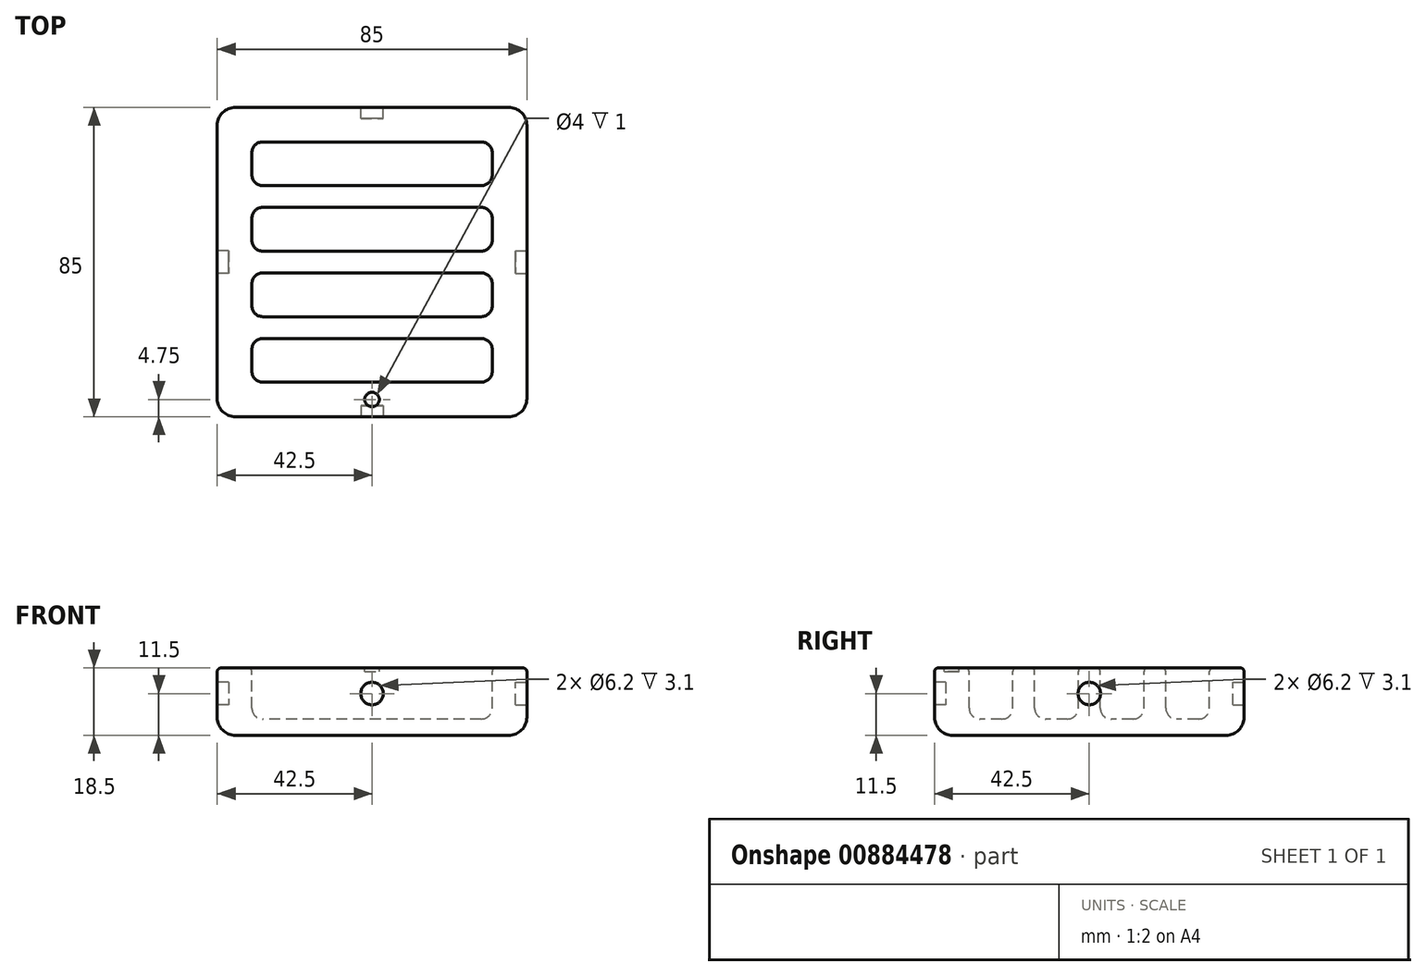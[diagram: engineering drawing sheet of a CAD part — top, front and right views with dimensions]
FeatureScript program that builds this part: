
annotation { "Feature Type Name" : "Feature", "Feature Type Description" : "" }
export const myFeature = defineFeature(function(context is Context, id is Id, definition is map)
    precondition{}
    {
        {
            var Q0;
            Q0=qCreatedBy(makeId("Top.planeOp"),FACE);
            var sketch = newSketch(context, id + "F0", { "sketchPlane" : qUnion([Q0])});
            skLineSegment(sketch, "E0.bottom", {"start": v(-42.5, 42.5) * mm, "end": v(42.5, 42.5) * mm});
            skLineSegment(sketch, "E0.top", {"start": v(-42.5, -42.5) * mm, "end": v(42.5, -42.5) * mm});
            skLineSegment(sketch, "E0.left", {"start": v(-42.5, 42.5) * mm, "end": v(-42.5, -42.5) * mm});
            skLineSegment(sketch, "E0.right", {"start": v(42.5, 42.5) * mm, "end": v(42.5, -42.5) * mm});
            skLineSegment(sketch, "E1.bottom", {"start": v(-30, 33) * mm, "end": v(30, 33) * mm});
            skLineSegment(sketch, "E1.top", {"start": v(-30, 21) * mm, "end": v(30, 21) * mm});
            skLineSegment(sketch, "E1.left", {"start": v(-33, 30) * mm, "end": v(-33, 24) * mm});
            skLineSegment(sketch, "E1.right", {"start": v(33, 30) * mm, "end": v(33, 24) * mm});
            skLineSegment(sketch, "E2.direction1", {"start": v(-33, 21) * mm, "end": v(-9.74, 21) * mm, "construction": true});
            skPoint(sketch, "E3.visualSharp", {"position": v(-33, 33) * mm});
            skArc(sketch, "E3.filletArc", {"start": v(-30, 33) * mm, "mid": v(-32.12, 32.12) * mm, "end": v(-33, 30) * mm});
            skPoint(sketch, "E4.visualSharp", {"position": v(33, 33) * mm});
            skArc(sketch, "E4.filletArc", {"start": v(33, 30) * mm, "mid": v(32.12, 32.12) * mm, "end": v(30, 33) * mm});
            skPoint(sketch, "E5.visualSharp", {"position": v(33, 21) * mm});
            skArc(sketch, "E5.filletArc", {"start": v(30, 21) * mm, "mid": v(32.12, 21.88) * mm, "end": v(33, 24) * mm});
            skPoint(sketch, "E6.visualSharp", {"position": v(-33, 21) * mm});
            skArc(sketch, "E6.filletArc", {"start": v(-33, 24) * mm, "mid": v(-32.12, 21.88) * mm, "end": v(-30, 21) * mm});
            skPoint(sketch, "E7.0.1.0", {"position": v(-33, 15) * mm});
            skLineSegment(sketch, "E7.0.1.1", {"start": v(-33, 3) * mm, "end": v(-9.74, 3) * mm, "construction": true});
            skLineSegment(sketch, "E7.0.1.2", {"start": v(-33, 12) * mm, "end": v(-33, 6) * mm});
            skPoint(sketch, "E7.0.1.3", {"position": v(33, 3) * mm});
            skArc(sketch, "E7.0.1.4", {"start": v(33, 12) * mm, "mid": v(32.12, 14.12) * mm, "end": v(30, 15) * mm});
            skLineSegment(sketch, "E7.0.1.5", {"start": v(-30, 15) * mm, "end": v(30, 15) * mm});
            skArc(sketch, "E7.0.1.6", {"start": v(-30, 15) * mm, "mid": v(-32.12, 14.12) * mm, "end": v(-33, 12) * mm});
            skLineSegment(sketch, "E7.0.1.7", {"start": v(33, 12) * mm, "end": v(33, 6) * mm});
            skPoint(sketch, "E7.0.1.8", {"position": v(33, 15) * mm});
            skLineSegment(sketch, "E7.0.1.9", {"start": v(-30, 3) * mm, "end": v(30, 3) * mm});
            skPoint(sketch, "E7.0.1.10", {"position": v(-33, 3) * mm});
            skArc(sketch, "E7.0.1.11", {"start": v(30, 3) * mm, "mid": v(32.12, 3.88) * mm, "end": v(33, 6) * mm});
            skArc(sketch, "E7.0.1.12", {"start": v(-33, 6) * mm, "mid": v(-32.12, 3.88) * mm, "end": v(-30, 3) * mm});
            skPoint(sketch, "E7.0.2.0", {"position": v(-33, -3) * mm});
            skLineSegment(sketch, "E7.0.2.1", {"start": v(-33, -15) * mm, "end": v(-9.74, -15) * mm, "construction": true});
            skLineSegment(sketch, "E7.0.2.2", {"start": v(-33, -6) * mm, "end": v(-33, -12) * mm});
            skPoint(sketch, "E7.0.2.3", {"position": v(33, -15) * mm});
            skArc(sketch, "E7.0.2.4", {"start": v(33, -6) * mm, "mid": v(32.12, -3.88) * mm, "end": v(30, -3) * mm});
            skLineSegment(sketch, "E7.0.2.5", {"start": v(-30, -3) * mm, "end": v(30, -3) * mm});
            skArc(sketch, "E7.0.2.6", {"start": v(-30, -3) * mm, "mid": v(-32.12, -3.88) * mm, "end": v(-33, -6) * mm});
            skLineSegment(sketch, "E7.0.2.7", {"start": v(33, -6) * mm, "end": v(33, -12) * mm});
            skPoint(sketch, "E7.0.2.8", {"position": v(33, -3) * mm});
            skLineSegment(sketch, "E7.0.2.9", {"start": v(-30, -15) * mm, "end": v(30, -15) * mm});
            skPoint(sketch, "E7.0.2.10", {"position": v(-33, -15) * mm});
            skArc(sketch, "E7.0.2.11", {"start": v(30, -15) * mm, "mid": v(32.12, -14.12) * mm, "end": v(33, -12) * mm});
            skArc(sketch, "E7.0.2.12", {"start": v(-33, -12) * mm, "mid": v(-32.12, -14.12) * mm, "end": v(-30, -15) * mm});
            skPoint(sketch, "E7.0.3.0", {"position": v(-33, -21) * mm});
            skLineSegment(sketch, "E7.0.3.1", {"start": v(-33, -33) * mm, "end": v(-9.74, -33) * mm, "construction": true});
            skLineSegment(sketch, "E7.0.3.2", {"start": v(-33, -24) * mm, "end": v(-33, -30) * mm});
            skPoint(sketch, "E7.0.3.3", {"position": v(33, -33) * mm});
            skArc(sketch, "E7.0.3.4", {"start": v(33, -24) * mm, "mid": v(32.12, -21.88) * mm, "end": v(30, -21) * mm});
            skLineSegment(sketch, "E7.0.3.5", {"start": v(-30, -21) * mm, "end": v(30, -21) * mm});
            skArc(sketch, "E7.0.3.6", {"start": v(-30, -21) * mm, "mid": v(-32.12, -21.88) * mm, "end": v(-33, -24) * mm});
            skLineSegment(sketch, "E7.0.3.7", {"start": v(33, -24) * mm, "end": v(33, -30) * mm});
            skPoint(sketch, "E7.0.3.8", {"position": v(33, -21) * mm});
            skLineSegment(sketch, "E7.0.3.9", {"start": v(-30, -33) * mm, "end": v(30, -33) * mm});
            skPoint(sketch, "E7.0.3.10", {"position": v(-33, -33) * mm});
            skArc(sketch, "E7.0.3.11", {"start": v(30, -33) * mm, "mid": v(32.12, -32.12) * mm, "end": v(33, -30) * mm});
            skArc(sketch, "E7.0.3.12", {"start": v(-33, -30) * mm, "mid": v(-32.12, -32.12) * mm, "end": v(-30, -33) * mm});
            skLineSegment(sketch, "E7.direction1", {"start": v(-33, 21) * mm, "end": v(-8, 21) * mm, "construction": true});
            skLineSegment(sketch, "E7.direction2", {"start": v(-33, 21) * mm, "end": v(-33, 3) * mm, "construction": true});
            skLineSegment(sketch, "E8", {"start": v(-42.5, 0) * mm, "end": v(42.5, 0) * mm, "construction": true});
            skLineSegment(sketch, "E9", {"start": v(0, -42.5) * mm, "end": v(0, 42.5) * mm, "construction": true});
            skCircle(sketch, "E10", {"center": v(0, -37.75) * mm, "radius": 2 * mm});
            skSolve(sketch);
        }
        {
            assignVariable(context, id + "F1", {"name" : "h", "anyValue" : 18.5});
        }
        {
            assignVariable(context, id + "F2", {"name" : "d", "anyValue" : 14});
        }
        {
            var Q0;
            Q0=makeQuery(id+"F0.imprint","IMPRINT",FACE,{"disambiguationData":[TD([[makeQuery(id+"F0.imprint","IMPRINT",EDGE,{"derivedFrom":sQuery(id+"F0.wireOp",EDGE,"E1.bottom")}),-1.0]])]});
            var Q1;
            Q1=makeQuery(id+"F0.imprint","IMPRINT",FACE,{"disambiguationData":[TD([[makeQuery(id+"F0.imprint","IMPRINT",EDGE,{"derivedFrom":sQuery(id+"F0.wireOp",EDGE,"E0.bottom")}),-1.0]])]});
            var Q2;
            Q2=makeQuery(id+"F0.imprint","IMPRINT",FACE,{"disambiguationData":[TD([[makeQuery(id+"F0.imprint","IMPRINT",EDGE,{"derivedFrom":sQuery(id+"F0.wireOp",EDGE,"E2.0.2.0")}),1.0]])]});
            var Q3;
            Q3=makeQuery(id+"F0.imprint","IMPRINT",FACE,{"disambiguationData":[TD([[makeQuery(id+"F0.imprint","IMPRINT",EDGE,{"derivedFrom":sQuery(id+"F0.wireOp",EDGE,"E2.0.3.0")}),1.0]])]});
            var Q4;
            Q4=makeQuery(id+"F0.imprint","IMPRINT",FACE,{"disambiguationData":[TD([[makeQuery(id+"F0.imprint","IMPRINT",EDGE,{"derivedFrom":sQuery(id+"F0.wireOp",EDGE,"E2.0.1.0")}),1.0]])]});
            var Q5;
            Q5=makeQuery(id+"F0.imprint","IMPRINT",FACE,{"disambiguationData":[TD([[makeQuery(id+"F0.imprint","IMPRINT",EDGE,{"derivedFrom":sQuery(id+"F0.wireOp",EDGE,"E7.0.1.2")}),1.0]])]});
            var Q6;
            Q6=makeQuery(id+"F0.imprint","IMPRINT",FACE,{"disambiguationData":[TD([[makeQuery(id+"F0.imprint","IMPRINT",EDGE,{"derivedFrom":sQuery(id+"F0.wireOp",EDGE,"E7.0.2.2")}),1.0]])]});
            var Q7;
            Q7=makeQuery(id+"F0.imprint","IMPRINT",FACE,{"disambiguationData":[TD([[makeQuery(id+"F0.imprint","IMPRINT",EDGE,{"derivedFrom":sQuery(id+"F0.wireOp",EDGE,"E7.0.3.2")}),1.0]])]});
            var Q8;
            Q8=makeQuery(id+"F0.imprint","IMPRINT",FACE,{"disambiguationData":[TD([[makeQuery(id+"F0.imprint","IMPRINT",EDGE,{"derivedFrom":sQuery(id+"F0.wireOp",EDGE,"E10")}),1.0]])]});
            extrude(context, id + "F3", {"entities" : qUnion([Q0, Q1, Q2, Q3, Q4, Q5, Q6, Q7, Q8]), "depth" : (getVariable(context, 'h')) * mm, "offsetDistance" : 25 * mm});
        }
        {
            var Q0;
            Q0=makeQuery(id+"F0.imprint","IMPRINT",FACE,{"disambiguationData":[TD([[makeQuery(id+"F0.imprint","IMPRINT",EDGE,{"derivedFrom":sQuery(id+"F0.wireOp",EDGE,"E1.bottom")}),-1.0]])]});
            var Q1;
            Q1=makeQuery(id+"F0.imprint","IMPRINT",FACE,{"disambiguationData":[TD([[makeQuery(id+"F0.imprint","IMPRINT",EDGE,{"derivedFrom":sQuery(id+"F0.wireOp",EDGE,"E2.0.1.0")}),1.0]])]});
            var Q2;
            Q2=makeQuery(id+"F0.imprint","IMPRINT",FACE,{"disambiguationData":[TD([[makeQuery(id+"F0.imprint","IMPRINT",EDGE,{"derivedFrom":sQuery(id+"F0.wireOp",EDGE,"E2.0.2.0")}),1.0]])]});
            var Q3;
            Q3=makeQuery(id+"F0.imprint","IMPRINT",FACE,{"disambiguationData":[TD([[makeQuery(id+"F0.imprint","IMPRINT",EDGE,{"derivedFrom":sQuery(id+"F0.wireOp",EDGE,"E2.0.3.0")}),1.0]])]});
            var Q4;
            Q4=makeQuery(id+"F0.imprint","IMPRINT",FACE,{"disambiguationData":[TD([[makeQuery(id+"F0.imprint","IMPRINT",EDGE,{"derivedFrom":sQuery(id+"F0.wireOp",EDGE,"E7.0.1.2")}),1.0]])]});
            var Q5;
            Q5=makeQuery(id+"F0.imprint","IMPRINT",FACE,{"disambiguationData":[TD([[makeQuery(id+"F0.imprint","IMPRINT",EDGE,{"derivedFrom":sQuery(id+"F0.wireOp",EDGE,"E7.0.2.2")}),1.0]])]});
            var Q6;
            Q6=makeQuery(id+"F0.imprint","IMPRINT",FACE,{"disambiguationData":[TD([[makeQuery(id+"F0.imprint","IMPRINT",EDGE,{"derivedFrom":sQuery(id+"F0.wireOp",EDGE,"E7.0.3.2")}),1.0]])]});
            extrude(context, id + "F4", {"entities" : qUnion([Q0, Q1, Q2, Q3, Q4, Q5, Q6]), "operationType" : NewBodyOperationType.REMOVE, "depth" : (getVariable(context, 'd')) * mm, "offsetDistance" : 25 * mm});
        }
        {
            var Q0;
            Q0=makeQuery(id+"F3.opExtrude","CAP_FACE",FACE,{"disambiguationData":[OSD([sQuery(id+"F0.wireOp",EDGE,"E0.bottom"),sQuery(id+"F0.wireOp",EDGE,"E0.top"),sQuery(id+"F0.wireOp",EDGE,"E0.left"),sQuery(id+"F0.wireOp",EDGE,"E0.right")])],"isStart":false});
            var Q1;
            Q1=makeQuery(id+"F3.opExtrude","SWEPT_EDGE",EDGE,{"disambiguationData":[OSD([sQuery(id+"F0.wireOp",EDGE,"E0.bottom"),sQuery(id+"F0.wireOp",EDGE,"E0.right")])]});
            var Q2;
            Q2=makeQuery(id+"F3.opExtrude","SWEPT_EDGE",EDGE,{"disambiguationData":[OSD([sQuery(id+"F0.wireOp",EDGE,"E0.bottom"),sQuery(id+"F0.wireOp",EDGE,"E0.left")])]});
            var Q3;
            Q3=makeQuery(id+"F3.opExtrude","SWEPT_EDGE",EDGE,{"disambiguationData":[OSD([sQuery(id+"F0.wireOp",EDGE,"E0.top"),sQuery(id+"F0.wireOp",EDGE,"E0.left")])]});
            var Q4;
            Q4=makeQuery(id+"F3.opExtrude","SWEPT_EDGE",EDGE,{"disambiguationData":[OSD([sQuery(id+"F0.wireOp",EDGE,"E0.top"),sQuery(id+"F0.wireOp",EDGE,"E0.right")])]});
            fillet(context, id + "F5", {"entities" : qUnion([Q0, Q1, Q2, Q3, Q4]), "radius" : 5 * mm, "tangentPropagation" : true, "allowEdgeOverflow" : false});
        }
        {
            var Q0;
            Q0=makeQuery(id+"F4.boolean.opBoolean","COPY",FACE,{"derivedFrom":makeQuery(id+"F4.opExtrude","CAP_FACE",FACE,{"disambiguationData":[OSD([sQuery(id+"F0.wireOp",EDGE,"E1.bottom"),sQuery(id+"F0.wireOp",EDGE,"E1.top"),sQuery(id+"F0.wireOp",EDGE,"E1.left"),sQuery(id+"F0.wireOp",EDGE,"E1.right"),sQuery(id+"F0.wireOp",EDGE,"E3.filletArc"),sQuery(id+"F0.wireOp",EDGE,"E4.filletArc"),sQuery(id+"F0.wireOp",EDGE,"E5.filletArc"),sQuery(id+"F0.wireOp",EDGE,"E6.filletArc")])],"isStart":false})});
            var Q1;
            Q1=makeQuery(id+"F4.boolean.opBoolean","COPY",FACE,{"derivedFrom":makeQuery(id+"F4.opExtrude","CAP_FACE",FACE,{"disambiguationData":[OSD([sQuery(id+"F0.wireOp",EDGE,"E7.0.1.2"),sQuery(id+"F0.wireOp",EDGE,"E7.0.1.4"),sQuery(id+"F0.wireOp",EDGE,"E7.0.1.5"),sQuery(id+"F0.wireOp",EDGE,"E7.0.1.6"),sQuery(id+"F0.wireOp",EDGE,"E7.0.1.7"),sQuery(id+"F0.wireOp",EDGE,"E7.0.1.9"),sQuery(id+"F0.wireOp",EDGE,"E7.0.1.11"),sQuery(id+"F0.wireOp",EDGE,"E7.0.1.12")])],"isStart":false})});
            var Q2;
            Q2=makeQuery(id+"F4.boolean.opBoolean","COPY",FACE,{"derivedFrom":makeQuery(id+"F4.opExtrude","CAP_FACE",FACE,{"disambiguationData":[OSD([sQuery(id+"F0.wireOp",EDGE,"E7.0.2.2"),sQuery(id+"F0.wireOp",EDGE,"E7.0.2.4"),sQuery(id+"F0.wireOp",EDGE,"E7.0.2.5"),sQuery(id+"F0.wireOp",EDGE,"E7.0.2.6"),sQuery(id+"F0.wireOp",EDGE,"E7.0.2.7"),sQuery(id+"F0.wireOp",EDGE,"E7.0.2.9"),sQuery(id+"F0.wireOp",EDGE,"E7.0.2.11"),sQuery(id+"F0.wireOp",EDGE,"E7.0.2.12")])],"isStart":false})});
            var Q3;
            Q3=makeQuery(id+"F4.boolean.opBoolean","COPY",FACE,{"derivedFrom":makeQuery(id+"F4.opExtrude","CAP_FACE",FACE,{"disambiguationData":[OSD([sQuery(id+"F0.wireOp",EDGE,"E7.0.3.2"),sQuery(id+"F0.wireOp",EDGE,"E7.0.3.4"),sQuery(id+"F0.wireOp",EDGE,"E7.0.3.5"),sQuery(id+"F0.wireOp",EDGE,"E7.0.3.6"),sQuery(id+"F0.wireOp",EDGE,"E7.0.3.7"),sQuery(id+"F0.wireOp",EDGE,"E7.0.3.9"),sQuery(id+"F0.wireOp",EDGE,"E7.0.3.11"),sQuery(id+"F0.wireOp",EDGE,"E7.0.3.12")])],"isStart":false})});
            fillet(context, id + "F6", {"entities" : qUnion([Q0, Q1, Q2, Q3]), "radius" : 3 * mm, "tangentPropagation" : true, "allowEdgeOverflow" : false});
        }
        {
            var Q0;
            Q0=makeQuery(id+"F3.opExtrude","CAP_FACE",FACE,{"disambiguationData":[OSD([sQuery(id+"F0.wireOp",EDGE,"E0.bottom"),sQuery(id+"F0.wireOp",EDGE,"E0.top"),sQuery(id+"F0.wireOp",EDGE,"E0.left"),sQuery(id+"F0.wireOp",EDGE,"E0.right")])],"isStart":true});
            fillet(context, id + "F7", {"entities" : qUnion([Q0]), "radius" : 1 * mm, "tangentPropagation" : true, "allowEdgeOverflow" : false});
        }
        {
            var Q0;
            Q0=makeQuery(id+"F3.opExtrude","SWEPT_FACE",FACE,{"disambiguationData":[OSD([sQuery(id+"F0.wireOp",EDGE,"E0.top")])]});
            var sketch = newSketch(context, id + "F8", { "sketchPlane" : qUnion([Q0])});
            skCircle(sketch, "E11", {"center": v(0, 7) * mm, "radius": 3.1 * mm});
            skSolve(sketch);
        }
        {
            var Q0;
            Q0=makeQuery(id+"F8.imprint","IMPRINT",FACE,{"disambiguationData":[TD([[makeQuery(id+"F8.imprint","IMPRINT",EDGE,{"derivedFrom":sQuery(id+"F8.wireOp",EDGE,"E11")}),1.0]])]});
            extrude(context, id + "F9", {"entities" : qUnion([Q0]), "operationType" : NewBodyOperationType.REMOVE, "oppositeDirection" : true, "depth" : 3.1 * mm, "offsetDistance" : 25 * mm});
        }
        {
            var Q0;
            Q0=makeQuery(id+"F3.opExtrude","SWEPT_FACE",FACE,{"disambiguationData":[OSD([sQuery(id+"F0.wireOp",EDGE,"E0.bottom")])]});
            var sketch = newSketch(context, id + "F10", { "sketchPlane" : qUnion([Q0])});
            skCircle(sketch, "E12", {"center": v(0, 7) * mm, "radius": 3.1 * mm});
            skSolve(sketch);
        }
        {
            var Q0;
            Q0=makeQuery(id+"F10.imprint","IMPRINT",FACE,{"disambiguationData":[TD([[makeQuery(id+"F10.imprint","IMPRINT",EDGE,{"derivedFrom":sQuery(id+"F10.wireOp",EDGE,"E12")}),1.0]])]});
            extrude(context, id + "F11", {"entities" : qUnion([Q0]), "operationType" : NewBodyOperationType.REMOVE, "oppositeDirection" : true, "depth" : 3.1 * mm, "offsetDistance" : 25 * mm});
        }
        {
            var Q0;
            Q0=makeQuery(id+"F3.opExtrude","SWEPT_FACE",FACE,{"disambiguationData":[OSD([sQuery(id+"F0.wireOp",EDGE,"E0.left")])]});
            var sketch = newSketch(context, id + "F12", { "sketchPlane" : qUnion([Q0])});
            skCircle(sketch, "E13", {"center": v(0, 7) * mm, "radius": 3.1 * mm});
            skSolve(sketch);
        }
        {
            var Q0;
            Q0=makeQuery(id+"F12.imprint","IMPRINT",FACE,{"disambiguationData":[TD([[makeQuery(id+"F12.imprint","IMPRINT",EDGE,{"derivedFrom":sQuery(id+"F12.wireOp",EDGE,"E13")}),1.0]])]});
            extrude(context, id + "F13", {"entities" : qUnion([Q0]), "operationType" : NewBodyOperationType.REMOVE, "oppositeDirection" : true, "depth" : 3.1 * mm, "offsetDistance" : 25 * mm});
        }
        {
            var Q0;
            Q0=makeQuery(id+"F3.opExtrude","SWEPT_FACE",FACE,{"disambiguationData":[OSD([sQuery(id+"F0.wireOp",EDGE,"E0.right")])]});
            var sketch = newSketch(context, id + "F14", { "sketchPlane" : qUnion([Q0])});
            skCircle(sketch, "E14", {"center": v(0, 7) * mm, "radius": 3.1 * mm});
            skSolve(sketch);
        }
        {
            var Q0;
            Q0=makeQuery(id+"F14.imprint","IMPRINT",FACE,{"disambiguationData":[TD([[makeQuery(id+"F14.imprint","IMPRINT",EDGE,{"derivedFrom":sQuery(id+"F14.wireOp",EDGE,"E14")}),1.0]])]});
            extrude(context, id + "F15", {"entities" : qUnion([Q0]), "operationType" : NewBodyOperationType.REMOVE, "oppositeDirection" : true, "depth" : 3.1 * mm, "offsetDistance" : 25 * mm});
        }
        {
            var Q0;
            Q0=makeQuery(id+"F0.imprint","IMPRINT",FACE,{"disambiguationData":[TD([[makeQuery(id+"F0.imprint","IMPRINT",EDGE,{"derivedFrom":sQuery(id+"F0.wireOp",EDGE,"E10")}),1.0]])]});
            extrude(context, id + "F16", {"entities" : qUnion([Q0]), "operationType" : NewBodyOperationType.REMOVE, "depth" : 1 * mm, "offsetDistance" : 25 * mm});
        }
        {
            var Q0;
            Q0=makeQuery(id+"F3.opExtrude","SWEPT_BODY",BODY,{"disambiguationData":[OSD([sQuery(id+"F0.wireOp",EDGE,"E0.bottom"),sQuery(id+"F0.wireOp",EDGE,"E0.top"),sQuery(id+"F0.wireOp",EDGE,"E0.left"),sQuery(id+"F0.wireOp",EDGE,"E0.right")])]});
            var Q1;
            Q1=sQuery(id+"F0.wireOp",EDGE,"E9");
            transform(context, id + "F17", {"entities" : qUnion([Q0]), "transformType" : TransformType.ROTATION, "transformAxis" : qUnion([Q1]), "angle" : 180 * degree, "makeCopy" : false});
        }
    });
